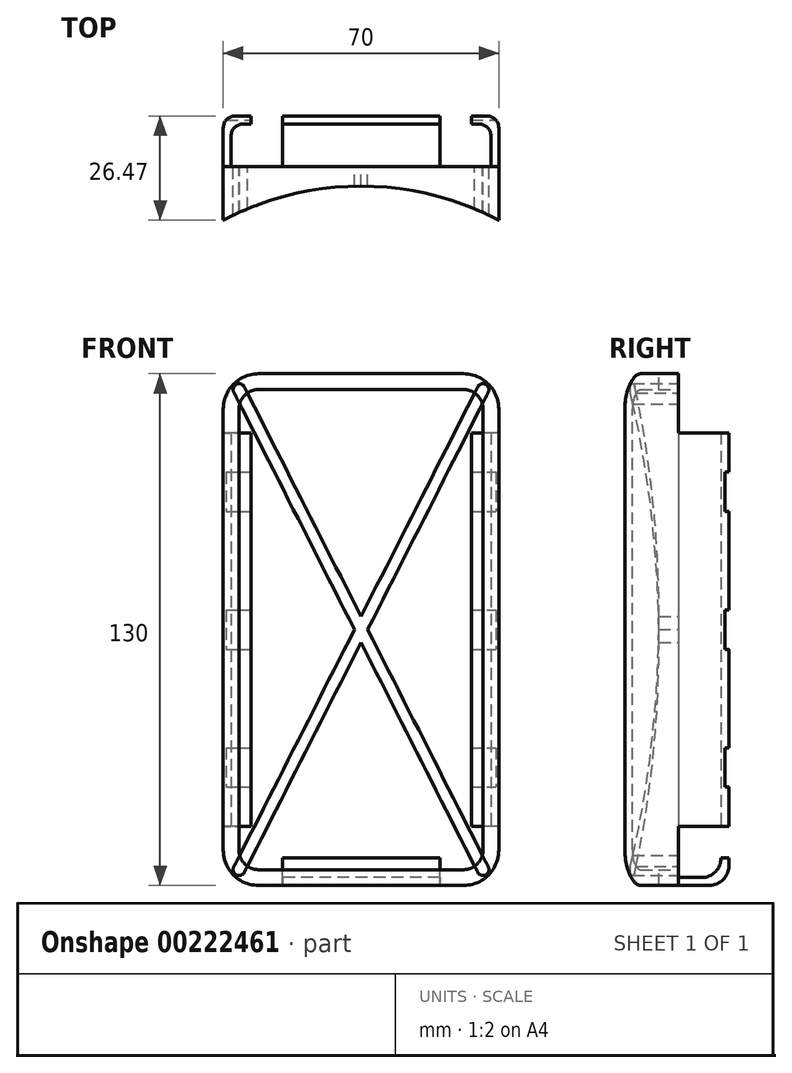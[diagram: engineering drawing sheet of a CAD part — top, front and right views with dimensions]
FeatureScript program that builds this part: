
annotation { "Feature Type Name" : "Feature", "Feature Type Description" : "" }
export const myFeature = defineFeature(function(context is Context, id is Id, definition is map)
    precondition{}
    {
        {
            var Q0;
            Q0=qCreatedBy(makeId("Front.planeOp"),FACE);
            var sketch = newSketch(context, id + "F0", { "sketchPlane" : qUnion([Q0])});
            skLineSegment(sketch, "E0.bottom", {"start": v(-26, 61) * mm, "end": v(26, 61) * mm});
            skLineSegment(sketch, "E0.top", {"start": v(-26, -61) * mm, "end": v(26, -61) * mm});
            skLineSegment(sketch, "E0.left", {"start": v(-31, 56) * mm, "end": v(-31, -56) * mm});
            skLineSegment(sketch, "E0.right", {"start": v(31, 56) * mm, "end": v(31, -56) * mm});
            skPoint(sketch, "E1.visualSharp", {"position": v(-31, 61) * mm});
            skArc(sketch, "E1.filletArc", {"start": v(-26, 61) * mm, "mid": v(-29.54, 59.54) * mm, "end": v(-31, 56) * mm});
            skPoint(sketch, "E2.visualSharp", {"position": v(31, 61) * mm});
            skArc(sketch, "E2.filletArc", {"start": v(31, 56) * mm, "mid": v(29.54, 59.54) * mm, "end": v(26, 61) * mm});
            skPoint(sketch, "E3.visualSharp", {"position": v(31, -61) * mm});
            skArc(sketch, "E3.filletArc", {"start": v(26, -61) * mm, "mid": v(29.54, -59.54) * mm, "end": v(31, -56) * mm});
            skPoint(sketch, "E4.visualSharp", {"position": v(-31, -61) * mm});
            skArc(sketch, "E4.filletArc", {"start": v(-31, -56) * mm, "mid": v(-29.54, -59.54) * mm, "end": v(-26, -61) * mm});
            skArc(sketch, "E5.0", {"start": v(-26, 65) * mm, "mid": v(-32.36, 62.36) * mm, "end": v(-35, 56) * mm});
            skLineSegment(sketch, "E5.1", {"start": v(-35, 56) * mm, "end": v(-35, -56) * mm});
            skLineSegment(sketch, "E5.2", {"start": v(-26, 65) * mm, "end": v(26, 65) * mm});
            skArc(sketch, "E5.3", {"start": v(-35, -56) * mm, "mid": v(-32.36, -62.36) * mm, "end": v(-26, -65) * mm});
            skArc(sketch, "E5.4", {"start": v(35, 56) * mm, "mid": v(32.36, 62.36) * mm, "end": v(26, 65) * mm});
            skLineSegment(sketch, "E5.5", {"start": v(35, 56) * mm, "end": v(35, -56) * mm});
            skArc(sketch, "E5.6", {"start": v(26, -65) * mm, "mid": v(32.36, -62.36) * mm, "end": v(35, -56) * mm});
            skLineSegment(sketch, "E5.7", {"start": v(-26, -65) * mm, "end": v(26, -65) * mm});
            skPoint(sketch, "E6.endSnap0", {"position": v(-29.54, -59.54) * mm});
            skLineSegment(sketch, "E7", {"start": v(-31, 61) * mm, "end": v(31, -61) * mm});
            skLineSegment(sketch, "E8", {"start": v(31, 61) * mm, "end": v(-31, -61) * mm});
            skArc(sketch, "E9.0.startCap", {"start": v(-32.34, 60.32) * mm, "mid": v(-31.68, 62.34) * mm, "end": v(-29.66, 61.68) * mm});
            skArc(sketch, "E9.0.endCap", {"start": v(32.34, -60.32) * mm, "mid": v(31.68, -62.34) * mm, "end": v(29.66, -61.68) * mm});
            skLineSegment(sketch, "E9.0.left", {"start": v(-29.66, 61.68) * mm, "end": v(32.34, -60.32) * mm});
            skLineSegment(sketch, "E9.0.right", {"start": v(-32.34, 60.32) * mm, "end": v(29.66, -61.68) * mm});
            skArc(sketch, "E9.1.startCap", {"start": v(29.66, 61.68) * mm, "mid": v(31.68, 62.34) * mm, "end": v(32.34, 60.32) * mm});
            skArc(sketch, "E9.1.endCap", {"start": v(-29.66, -61.68) * mm, "mid": v(-31.68, -62.34) * mm, "end": v(-32.34, -60.32) * mm});
            skLineSegment(sketch, "E9.1.left", {"start": v(32.34, 60.32) * mm, "end": v(-29.66, -61.68) * mm});
            skLineSegment(sketch, "E9.1.right", {"start": v(29.66, 61.68) * mm, "end": v(-32.34, -60.32) * mm});
            skSolve(sketch);
        }
        {
            var Q0;
            {var subQ1=sQuery(id+"F0.wireOp",EDGE,"E9.1.endCap");Q0=makeQuery(id+"F0.imprint","IMPRINT",FACE,{"disambiguationData":[TD([[makeQuery(id+"F0.imprint","IMPRINT",EDGE,{"derivedFrom":subQ1}),-1.0]])]});}
            var Q1;
            {var subQ0=sQuery(id+"F0.wireOp",EDGE,"E8");var subQ1=sQuery(id+"F0.wireOp",EDGE,"E4.filletArc");var subQ2=makeQuery(id+"F0.imprint","INTERSECT",VERTEX,{"derivedFrom":[subQ1,subQ0]});Q1=makeQuery(id+"F0.imprint","IMPRINT",FACE,{"disambiguationData":[TD([[makeQuery(id+"F0.imprint","IMPRINT",EDGE,{"disambiguationData":[TD([[subQ2,1.0]])],"derivedFrom":subQ1}),1.0]])]});}
            var Q2;
            {var subQ0=sQuery(id+"F0.wireOp",EDGE,"E8");var subQ1=sQuery(id+"F0.wireOp",EDGE,"E4.filletArc");var subQ2=makeQuery(id+"F0.imprint","INTERSECT",VERTEX,{"derivedFrom":[subQ1,subQ0]});Q2=makeQuery(id+"F0.imprint","IMPRINT",FACE,{"disambiguationData":[TD([[makeQuery(id+"F0.imprint","IMPRINT",EDGE,{"disambiguationData":[TD([[subQ2,-1.0]])],"derivedFrom":subQ1}),1.0]])]});}
            var Q3;
            {var subQ1=sQuery(id+"F0.wireOp",EDGE,"E9.0.startCap");Q3=makeQuery(id+"F0.imprint","IMPRINT",FACE,{"disambiguationData":[TD([[makeQuery(id+"F0.imprint","IMPRINT",EDGE,{"derivedFrom":subQ1}),-1.0]])]});}
            var Q4;
            {var subQ1=sQuery(id+"F0.wireOp",EDGE,"E9.1.startCap");Q4=makeQuery(id+"F0.imprint","IMPRINT",FACE,{"disambiguationData":[TD([[makeQuery(id+"F0.imprint","IMPRINT",EDGE,{"derivedFrom":subQ1}),-1.0]])]});}
            var Q5;
            {var subQ0=sQuery(id+"F0.wireOp",EDGE,"E9.0.endCap");Q5=makeQuery(id+"F0.imprint","IMPRINT",FACE,{"disambiguationData":[TD([[makeQuery(id+"F0.imprint","IMPRINT",EDGE,{"derivedFrom":subQ0}),-1.0]])]});}
            var Q6;
            {var subQ0=sQuery(id+"F0.wireOp",EDGE,"E7");var subQ1=sQuery(id+"F0.wireOp",EDGE,"E1.filletArc");var subQ2=makeQuery(id+"F0.imprint","INTERSECT",VERTEX,{"derivedFrom":[subQ1,subQ0]});Q6=makeQuery(id+"F0.imprint","IMPRINT",FACE,{"disambiguationData":[TD([[makeQuery(id+"F0.imprint","IMPRINT",EDGE,{"disambiguationData":[TD([[subQ2,1.0]])],"derivedFrom":subQ1}),1.0]])]});}
            var Q7;
            {var subQ0=sQuery(id+"F0.wireOp",EDGE,"E7");var subQ1=sQuery(id+"F0.wireOp",EDGE,"E1.filletArc");var subQ2=makeQuery(id+"F0.imprint","INTERSECT",VERTEX,{"derivedFrom":[subQ1,subQ0]});Q7=makeQuery(id+"F0.imprint","IMPRINT",FACE,{"disambiguationData":[TD([[makeQuery(id+"F0.imprint","IMPRINT",EDGE,{"disambiguationData":[TD([[subQ2,-1.0]])],"derivedFrom":subQ1}),1.0]])]});}
            var Q8;
            {var subQ0=sQuery(id+"F0.wireOp",EDGE,"E8");var subQ1=sQuery(id+"F0.wireOp",EDGE,"E2.filletArc");var subQ2=makeQuery(id+"F0.imprint","INTERSECT",VERTEX,{"derivedFrom":[subQ1,subQ0]});Q8=makeQuery(id+"F0.imprint","IMPRINT",FACE,{"disambiguationData":[TD([[makeQuery(id+"F0.imprint","IMPRINT",EDGE,{"disambiguationData":[TD([[subQ2,1.0]])],"derivedFrom":subQ1}),1.0]])]});}
            var Q9;
            {var subQ0=sQuery(id+"F0.wireOp",EDGE,"E8");var subQ1=sQuery(id+"F0.wireOp",EDGE,"E2.filletArc");var subQ2=makeQuery(id+"F0.imprint","INTERSECT",VERTEX,{"derivedFrom":[subQ1,subQ0]});Q9=makeQuery(id+"F0.imprint","IMPRINT",FACE,{"disambiguationData":[TD([[makeQuery(id+"F0.imprint","IMPRINT",EDGE,{"disambiguationData":[TD([[subQ2,-1.0]])],"derivedFrom":subQ1}),1.0]])]});}
            var Q10;
            {var subQ0=sQuery(id+"F0.wireOp",EDGE,"E7");var subQ1=sQuery(id+"F0.wireOp",EDGE,"E3.filletArc");var subQ2=makeQuery(id+"F0.imprint","INTERSECT",VERTEX,{"derivedFrom":[subQ1,subQ0]});Q10=makeQuery(id+"F0.imprint","IMPRINT",FACE,{"disambiguationData":[TD([[makeQuery(id+"F0.imprint","IMPRINT",EDGE,{"disambiguationData":[TD([[subQ2,1.0]])],"derivedFrom":subQ1}),1.0]])]});}
            var Q11;
            {var subQ0=sQuery(id+"F0.wireOp",EDGE,"E7");var subQ1=sQuery(id+"F0.wireOp",EDGE,"E3.filletArc");var subQ2=makeQuery(id+"F0.imprint","INTERSECT",VERTEX,{"derivedFrom":[subQ1,subQ0]});Q11=makeQuery(id+"F0.imprint","IMPRINT",FACE,{"disambiguationData":[TD([[makeQuery(id+"F0.imprint","IMPRINT",EDGE,{"disambiguationData":[TD([[subQ2,-1.0]])],"derivedFrom":subQ1}),1.0]])]});}
            var Q12;
            {var subQ0=sQuery(id+"F0.wireOp",EDGE,"E9.1.right");var subQ1=sQuery(id+"F0.wireOp",EDGE,"E7");var subQ2=makeQuery(id+"F0.imprint","INTERSECT",VERTEX,{"derivedFrom":[subQ1,subQ0]});Q12=makeQuery(id+"F0.imprint","IMPRINT",FACE,{"disambiguationData":[TD([[makeQuery(id+"F0.imprint","IMPRINT",EDGE,{"disambiguationData":[TD([[subQ2,-1.0]])],"derivedFrom":subQ1}),1.0]])]});}
            var Q13;
            {var subQ0=sQuery(id+"F0.wireOp",EDGE,"E9.1.right");var subQ1=sQuery(id+"F0.wireOp",EDGE,"E7");var subQ2=makeQuery(id+"F0.imprint","INTERSECT",VERTEX,{"derivedFrom":[subQ1,subQ0]});Q13=makeQuery(id+"F0.imprint","IMPRINT",FACE,{"disambiguationData":[TD([[makeQuery(id+"F0.imprint","IMPRINT",EDGE,{"disambiguationData":[TD([[subQ2,-1.0]])],"derivedFrom":subQ1}),-1.0]])]});}
            var Q14;
            {var subQ0=sQuery(id+"F0.wireOp",EDGE,"E8");var subQ1=sQuery(id+"F0.wireOp",EDGE,"E7");var subQ2=makeQuery(id+"F0.imprint","INTERSECT",VERTEX,{"derivedFrom":[subQ1,subQ0]});Q14=makeQuery(id+"F0.imprint","IMPRINT",FACE,{"disambiguationData":[TD([[makeQuery(id+"F0.imprint","IMPRINT",EDGE,{"disambiguationData":[TD([[subQ2,-1.0]])],"derivedFrom":subQ1}),1.0]])]});}
            var Q15;
            {var subQ0=sQuery(id+"F0.wireOp",EDGE,"E8");var subQ1=sQuery(id+"F0.wireOp",EDGE,"E7");var subQ2=makeQuery(id+"F0.imprint","INTERSECT",VERTEX,{"derivedFrom":[subQ1,subQ0]});Q15=makeQuery(id+"F0.imprint","IMPRINT",FACE,{"disambiguationData":[TD([[makeQuery(id+"F0.imprint","IMPRINT",EDGE,{"disambiguationData":[TD([[subQ2,-1.0]])],"derivedFrom":subQ1}),-1.0]])]});}
            var Q16;
            {var subQ16=sQuery(id+"F0.wireOp",EDGE,"E0.bottom");Q16=makeQuery(id+"F0.imprint","IMPRINT",FACE,{"disambiguationData":[TD([[makeQuery(id+"F0.imprint","IMPRINT",EDGE,{"derivedFrom":subQ16}),1.0]])]});}
            extrude(context, id + "F1", {"entities" : qUnion([Q0, Q1, Q2, Q3, Q4, Q5, Q6, Q7, Q8, Q9, Q10, Q11, Q12, Q13, Q14, Q15, Q16]), "depth" : 25 * mm});
        }
        {
            var Q0;
            Q0=qCreatedBy(makeId("Top.planeOp"),FACE);
            var sketch = newSketch(context, id + "F2", { "sketchPlane" : qUnion([Q0])});
            skPoint(sketch, "E10", {"position": v(0, -80) * mm});
            skCircle(sketch, "E11", {"center": v(0, -80) * mm, "radius": 75 * mm});
            skSolve(sketch);
        }
        {
            var Q0;
            Q0 = qSketchRegion(id + "F2", true);
            extrude(context, id + "F3", {"entities" : qUnion([Q0]), "operationType" : NewBodyOperationType.REMOVE, "endBound" : BoundingType.THROUGH_ALL, "oppositeDirection" : true, "depth" : 25 * mm, "hasSecondDirection" : true, "secondDirectionBound" : SecondDirectionBoundingType.THROUGH_ALL, "secondDirectionOppositeDirection" : false, "secondDirectionDepth" : 25 * mm});
        }
        {
            var Q0;
            Q0=qCreatedBy(makeId("Top.planeOp"),FACE);
            var sketch = newSketch(context, id + "F4", { "sketchPlane" : qUnion([Q0])});
            skLineSegment(sketch, "E12", {"start": v(-35, 0) * mm, "end": v(-35, 9.8) * mm});
            skLineSegment(sketch, "E13", {"start": v(-32, 12.8) * mm, "end": v(-28, 12.8) * mm});
            skLineSegment(sketch, "E14", {"start": v(-28, 12.8) * mm, "end": v(-28, 10.8) * mm});
            skLineSegment(sketch, "E15", {"start": v(-28, 10.8) * mm, "end": v(-30, 10.8) * mm});
            skLineSegment(sketch, "E16", {"start": v(-33, 7.8) * mm, "end": v(-33, 0) * mm});
            skLineSegment(sketch, "E17.MirrorCS", {"start": v(28, 12.8) * mm, "end": v(28, 10.8) * mm});
            skLineSegment(sketch, "E18.MirrorCS", {"start": v(32, 12.8) * mm, "end": v(28, 12.8) * mm});
            skLineSegment(sketch, "E19.MirrorCS", {"start": v(33, 7.8) * mm, "end": v(33, 0) * mm});
            skLineSegment(sketch, "E20.MirrorCS", {"start": v(28, 10.8) * mm, "end": v(30, 10.8) * mm});
            skLineSegment(sketch, "E21.MirrorCS", {"start": v(35, 0) * mm, "end": v(35, 9.8) * mm});
            skLineSegment(sketch, "E22", {"start": v(-35, 0) * mm, "end": v(-33, 0) * mm});
            skLineSegment(sketch, "E23", {"start": v(35, 0) * mm, "end": v(33, 0) * mm});
            skPoint(sketch, "E24.visualSharp", {"position": v(-35, 12.8) * mm});
            skArc(sketch, "E24.filletArc", {"start": v(-32, 12.8) * mm, "mid": v(-34.12, 11.92) * mm, "end": v(-35, 9.8) * mm});
            skPoint(sketch, "E25.visualSharp", {"position": v(-33, 10.8) * mm});
            skArc(sketch, "E25.filletArc", {"start": v(-30, 10.8) * mm, "mid": v(-32.12, 9.92) * mm, "end": v(-33, 7.8) * mm});
            skPoint(sketch, "E26.visualSharp", {"position": v(35, 12.8) * mm});
            skArc(sketch, "E26.filletArc", {"start": v(35, 9.8) * mm, "mid": v(34.12, 11.92) * mm, "end": v(32, 12.8) * mm});
            skPoint(sketch, "E27.visualSharp", {"position": v(33, 10.8) * mm});
            skArc(sketch, "E27.filletArc", {"start": v(33, 7.8) * mm, "mid": v(32.12, 9.92) * mm, "end": v(30, 10.8) * mm});
            skSolve(sketch);
        }
        {
            var Q0;
            Q0=makeQuery(id+"F4.imprint","IMPRINT",FACE,{"disambiguationData":[TD([[makeQuery(id+"F4.imprint","IMPRINT",EDGE,{"derivedFrom":sQuery(id+"F4.wireOp",EDGE,"E12")}),-1.0]])]});
            var Q1;
            Q1=makeQuery(id+"F4.imprint","IMPRINT",FACE,{"disambiguationData":[TD([[makeQuery(id+"F4.imprint","IMPRINT",EDGE,{"derivedFrom":sQuery(id+"F4.wireOp",EDGE,"E17.MirrorCS")}),1.0]])]});
            extrude(context, id + "F5", {"entities" : qUnion([Q0, Q1]), "operationType" : NewBodyOperationType.ADD, "endBound" : BoundingType.SYMMETRIC, "depth" : 100 * mm});
        }
        {
            var Q0;
            Q0=qCreatedBy(makeId("Right.planeOp"),FACE);
            var sketch = newSketch(context, id + "F6", { "sketchPlane" : qUnion([Q0])});
            skLineSegment(sketch, "E28", {"start": v(0, -65) * mm, "end": v(7.8, -65) * mm});
            skLineSegment(sketch, "E29", {"start": v(12.8, -60) * mm, "end": v(12.8, -58) * mm});
            skLineSegment(sketch, "E30", {"start": v(12.8, -58) * mm, "end": v(10.8, -58) * mm});
            skLineSegment(sketch, "E31", {"start": v(10.8, -58) * mm, "end": v(10.8, -58) * mm});
            skLineSegment(sketch, "E32", {"start": v(5.8, -63) * mm, "end": v(0, -63) * mm});
            skLineSegment(sketch, "E33", {"start": v(0, -63) * mm, "end": v(0, -65) * mm});
            skPoint(sketch, "E34.visualSharp", {"position": v(12.8, -65) * mm});
            skArc(sketch, "E34.filletArc", {"start": v(7.8, -65) * mm, "mid": v(11.34, -63.54) * mm, "end": v(12.8, -60) * mm});
            skPoint(sketch, "E35.visualSharp", {"position": v(10.8, -63) * mm});
            skArc(sketch, "E35.filletArc", {"start": v(5.8, -63) * mm, "mid": v(9.34, -61.54) * mm, "end": v(10.8, -58) * mm});
            skSolve(sketch);
        }
        {
            var Q0;
            Q0=makeQuery(id+"F6.imprint","IMPRINT",FACE,{"disambiguationData":[TD([[makeQuery(id+"F6.imprint","IMPRINT",EDGE,{"derivedFrom":sQuery(id+"F6.wireOp",EDGE,"E28")}),1.0]])]});
            extrude(context, id + "F7", {"entities" : qUnion([Q0]), "operationType" : NewBodyOperationType.ADD, "endBound" : BoundingType.SYMMETRIC, "depth" : 40 * mm});
        }
        {
            var Q0;
            Q0=qCreatedBy(makeId("Right.planeOp"),FACE);
            var sketch = newSketch(context, id + "F8", { "sketchPlane" : qUnion([Q0])});
            skLineSegment(sketch, "E36.bottom", {"start": v(11.8, 40) * mm, "end": v(12.8, 40) * mm});
            skLineSegment(sketch, "E36.top", {"start": v(11.8, 30) * mm, "end": v(12.8, 30) * mm});
            skLineSegment(sketch, "E36.left", {"start": v(11.8, 40) * mm, "end": v(11.8, 30) * mm});
            skLineSegment(sketch, "E36.right", {"start": v(12.8, 40) * mm, "end": v(12.8, 30) * mm});
            skLineSegment(sketch, "E37.MirrorCS", {"start": v(12.8, -40) * mm, "end": v(12.8, -30) * mm});
            skLineSegment(sketch, "E38.MirrorCS", {"start": v(11.8, -40) * mm, "end": v(11.8, -30) * mm});
            skLineSegment(sketch, "E39.MirrorCS", {"start": v(11.8, -30) * mm, "end": v(12.8, -30) * mm});
            skLineSegment(sketch, "E40.MirrorCS", {"start": v(11.8, -40) * mm, "end": v(12.8, -40) * mm});
            skLineSegment(sketch, "E41.top", {"start": v(11.8, 5) * mm, "end": v(12.8, 5) * mm});
            skLineSegment(sketch, "E41.right", {"start": v(12.8, 0) * mm, "end": v(12.8, 5) * mm});
            skLineSegment(sketch, "E42.MirrorCS", {"start": v(12.8, 0) * mm, "end": v(12.8, -5) * mm});
            skLineSegment(sketch, "E43.MirrorCS", {"start": v(11.8, -5) * mm, "end": v(12.8, -5) * mm});
            skLineSegment(sketch, "E44", {"start": v(11.8, 5) * mm, "end": v(11.8, -5) * mm});
            skSolve(sketch);
        }
        {
            var Q0;
            Q0=makeQuery(id+"F8.imprint","IMPRINT",FACE,{"disambiguationData":[TD([[makeQuery(id+"F8.imprint","IMPRINT",EDGE,{"derivedFrom":sQuery(id+"F8.wireOp",EDGE,"E36.bottom")}),-1.0]])]});
            var Q1;
            Q1=makeQuery(id+"F8.imprint","IMPRINT",FACE,{"disambiguationData":[TD([[makeQuery(id+"F8.imprint","IMPRINT",EDGE,{"derivedFrom":sQuery(id+"F8.wireOp",EDGE,"E37.MirrorCS")}),1.0]])]});
            var Q2;
            Q2=makeQuery(id+"F8.imprint","IMPRINT",FACE,{"disambiguationData":[TD([[makeQuery(id+"F8.imprint","IMPRINT",EDGE,{"derivedFrom":sQuery(id+"F8.wireOp",EDGE,"E41.top")}),-1.0]])]});
            extrude(context, id + "F9", {"entities" : qUnion([Q0, Q1, Q2]), "operationType" : NewBodyOperationType.REMOVE, "endBound" : BoundingType.THROUGH_ALL, "oppositeDirection" : true, "depth" : 25 * mm, "hasSecondDirection" : true, "secondDirectionBound" : SecondDirectionBoundingType.THROUGH_ALL, "secondDirectionOppositeDirection" : false, "secondDirectionDepth" : 25 * mm});
        }
    });
